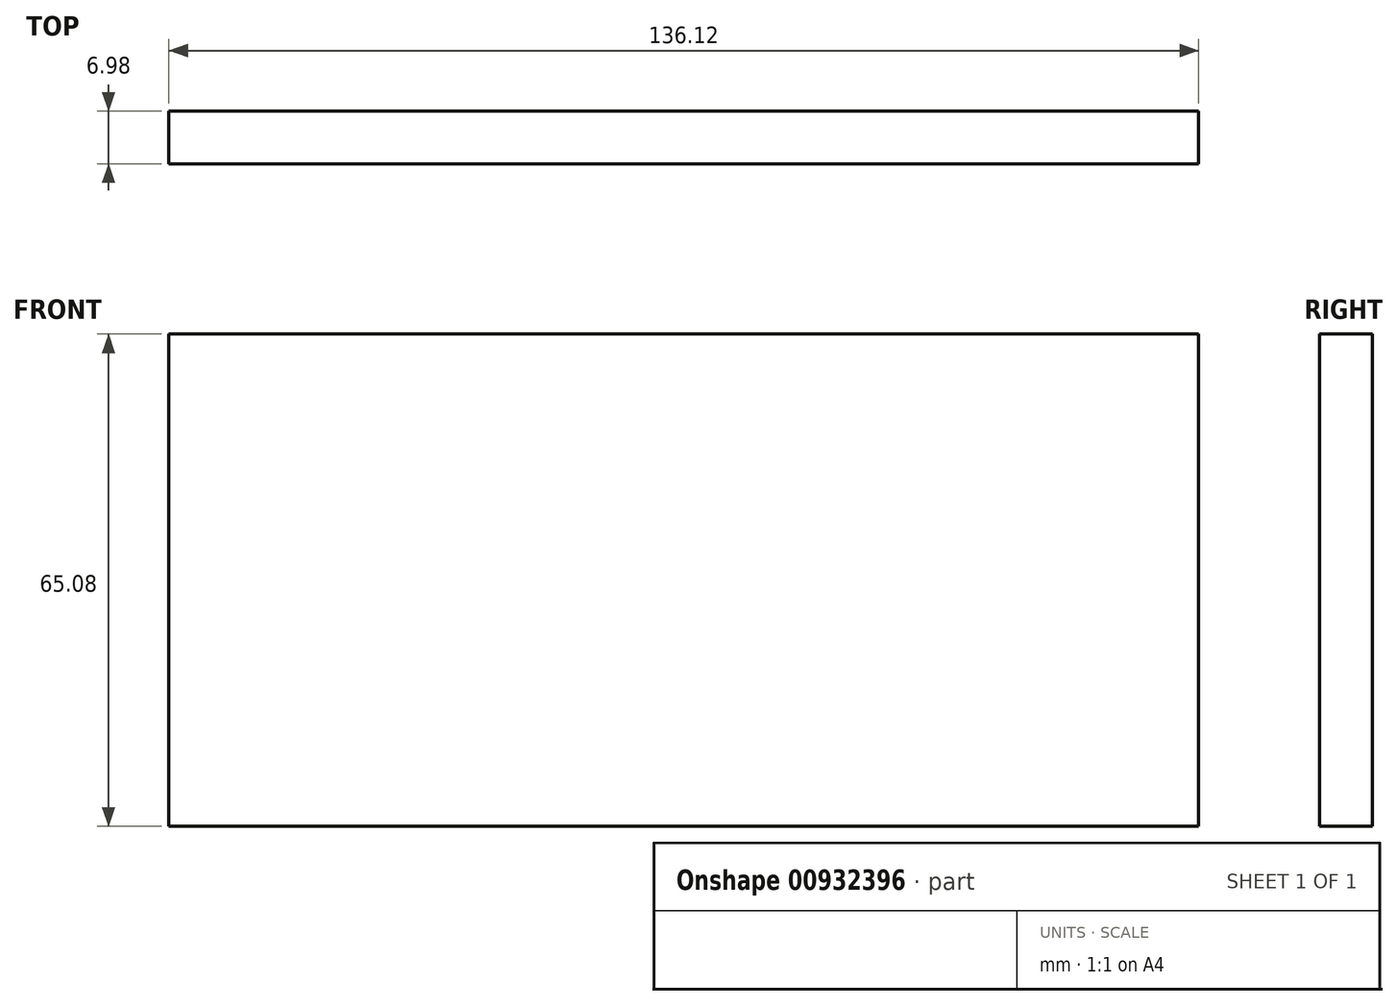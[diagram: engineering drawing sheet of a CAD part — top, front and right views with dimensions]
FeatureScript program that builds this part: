
annotation { "Feature Type Name" : "Feature", "Feature Type Description" : "" }
export const myFeature = defineFeature(function(context is Context, id is Id, definition is map)
    precondition{}
    {
        {
            var Q0;
            Q0=qCreatedBy(makeId("Front.planeOp"),FACE);
            var sketch = newSketch(context, id + "F0", { "sketchPlane" : qUnion([Q0])});
            skLineSegment(sketch, "E0.bottom", {"start": v(68.06, 32.54) * mm, "end": v(-68.06, 32.54) * mm});
            skLineSegment(sketch, "E0.top", {"start": v(68.06, -32.54) * mm, "end": v(-68.06, -32.54) * mm});
            skLineSegment(sketch, "E0.left", {"start": v(68.06, 32.54) * mm, "end": v(68.06, -32.54) * mm});
            skLineSegment(sketch, "E0.right", {"start": v(-68.06, 32.54) * mm, "end": v(-68.06, -32.54) * mm});
            skPoint(sketch, "E0.middle", {"position": v(0, 0) * mm});
            skSolve(sketch);
        }
        {
            var Q0;
            Q0 = qSketchRegion(id + "F0", true);
            extrude(context, id + "F1", {"entities" : qUnion([Q0]), "endBound" : BoundingType.SYMMETRIC, "depth" : 7 * mm, "offsetDistance" : 25.4 * mm});
        }
    });
